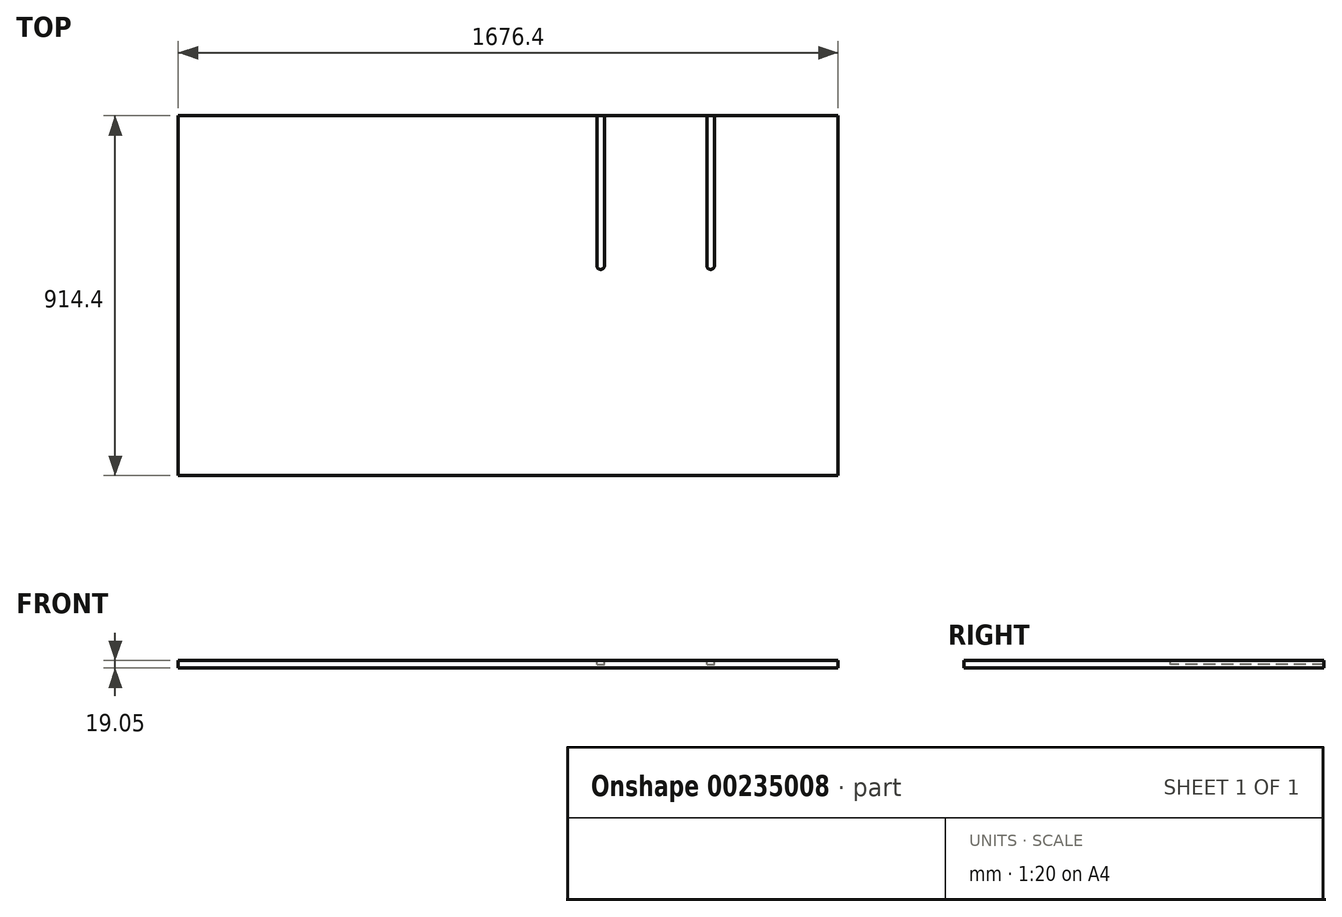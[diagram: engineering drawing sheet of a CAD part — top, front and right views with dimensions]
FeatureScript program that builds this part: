
annotation { "Feature Type Name" : "Feature", "Feature Type Description" : "" }
export const myFeature = defineFeature(function(context is Context, id is Id, definition is map)
    precondition{}
    {
        {
            var Q0;
            Q0=qCreatedBy(makeId("Top.planeOp"),FACE);
            var sketch = newSketch(context, id + "F0", { "sketchPlane" : qUnion([Q0])});
            skLineSegment(sketch, "E0.bottom", {"start": v(-838.2, 457.2) * mm, "end": v(838.2, 457.2) * mm});
            skLineSegment(sketch, "E0.top", {"start": v(-838.2, -457.2) * mm, "end": v(838.2, -457.2) * mm});
            skLineSegment(sketch, "E0.left", {"start": v(-838.2, 457.2) * mm, "end": v(-838.2, -457.2) * mm});
            skLineSegment(sketch, "E0.right", {"start": v(838.2, 457.2) * mm, "end": v(838.2, -457.2) * mm});
            skSolve(sketch);
        }
        {
            var Q0;
            Q0=makeQuery(id+"F0.imprint","IMPRINT",FACE,{"disambiguationData":[TD([[makeQuery(id+"F0.imprint","IMPRINT",EDGE,{"derivedFrom":sQuery(id+"F0.wireOp",EDGE,"E0.bottom")}),-1.0]])]});
            extrude(context, id + "F1", {"entities" : qUnion([Q0]), "depth" : 19.05 * mm});
        }
        {
            var Q0;
            Q0=makeQuery(id+"F1.opExtrude","CAP_FACE",FACE,{"disambiguationData":[OSD([sQuery(id+"F0.wireOp",EDGE,"E0.bottom"),sQuery(id+"F0.wireOp",EDGE,"E0.top"),sQuery(id+"F0.wireOp",EDGE,"E0.left"),sQuery(id+"F0.wireOp",EDGE,"E0.right")])],"isStart":false});
            var sketch = newSketch(context, id + "F2", { "sketchPlane" : qUnion([Q0])});
            skLineSegment(sketch, "E1.bottom", {"start": v(523.88, 457.2) * mm, "end": v(504.83, 457.2) * mm});
            skLineSegment(sketch, "E1.top", {"start": v(523.88, 76.2) * mm, "end": v(504.83, 76.2) * mm, "construction": true});
            skLineSegment(sketch, "E1.left", {"start": v(523.88, 457.2) * mm, "end": v(523.88, 76.2) * mm});
            skLineSegment(sketch, "E1.right", {"start": v(504.82, 457.2) * mm, "end": v(504.83, 76.2) * mm});
            skArc(sketch, "E2", {"start": v(504.83, 76.2) * mm, "mid": v(514.35, 66.67) * mm, "end": v(523.88, 76.2) * mm});
            skLineSegment(sketch, "E3.bottom", {"start": v(244.47, 457.2) * mm, "end": v(225.42, 457.2) * mm});
            skLineSegment(sketch, "E3.top", {"start": v(244.48, 76.2) * mm, "end": v(225.43, 76.2) * mm, "construction": true});
            skLineSegment(sketch, "E3.left", {"start": v(244.47, 457.2) * mm, "end": v(244.48, 76.2) * mm});
            skLineSegment(sketch, "E3.right", {"start": v(225.42, 457.2) * mm, "end": v(225.43, 76.2) * mm});
            skArc(sketch, "E4", {"start": v(225.43, 76.2) * mm, "mid": v(234.95, 66.67) * mm, "end": v(244.48, 76.2) * mm});
            skSolve(sketch);
        }
        {
            var Q0;
            Q0=makeQuery(id+"F2.imprint","IMPRINT",FACE,{"disambiguationData":[TD([[makeQuery(id+"F2.imprint","IMPRINT",EDGE,{"derivedFrom":sQuery(id+"F2.wireOp",EDGE,"E1.bottom")}),-1.0]])]});
            var Q1;
            Q1=makeQuery(id+"F2.imprint","IMPRINT",FACE,{"disambiguationData":[TD([[makeQuery(id+"F2.imprint","IMPRINT",EDGE,{"derivedFrom":sQuery(id+"F2.wireOp",EDGE,"E3.bottom")}),-1.0]])]});
            extrude(context, id + "F3", {"entities" : qUnion([Q0, Q1]), "operationType" : NewBodyOperationType.REMOVE, "oppositeDirection" : true, "depth" : 9.52 * mm});
        }
    });
